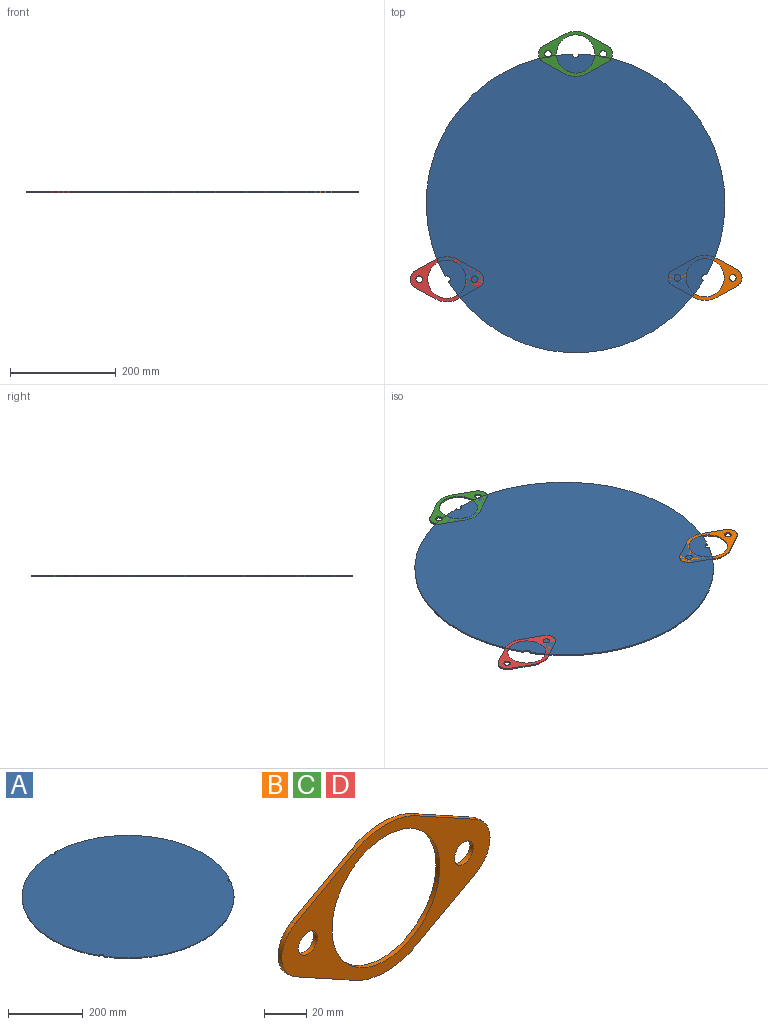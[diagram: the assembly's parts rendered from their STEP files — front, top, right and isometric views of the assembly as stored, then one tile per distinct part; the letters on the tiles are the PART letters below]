
ASSEMBLY  parts=4 mates=5
PART A: 8 faces, bbox 565.8x565.7x2.5 mm
  f0: cylinder r=6.35mm len=11.82mm, axis (0,0,-1), area 50.3mm2, adj f1,f5,f6,f7
  f1: cylinder r=282.91mm len=418.29mm, axis (0,0,-1), area 1471.4mm2, adj f0,f2,f6,f7
  f2: cylinder r=6.35mm len=12.7mm, axis (0,0,-1), area 50.3mm2, adj f1,f3,f6,f7
  f3: cylinder r=282.91mm len=421.07mm, axis (0,0,-1), area 1479.5mm2, adj f2,f4,f6,f7
  f4: cylinder r=6.35mm len=11.78mm, axis (0,0,-1), area 50.3mm2, adj f3,f5,f6,f7
  f5: cylinder r=282.91mm len=482.44mm, axis (0,0,-1), area 1467.4mm2, adj f0,f4,f6,f7
  f6: plane 565.82x565.75mm, normal (0,0,1), area 251257.3mm2, adj f0,f1,f2,f3,f4,f5
  f7: plane 565.82x565.75mm, normal (0,0,-1), area 251257.3mm2, adj f0,f1,f2,f3,f4,f5
PART B: 13 faces, bbox 139.7x2.5x85.6 mm
  f0: cylinder r=17.53mm len=30.69mm, axis (0,1,0), area 95mm2, adj f1,f9,f11,f12
  f1: plane 40.12x22.13mm, normal (0.48,0,0.88), area 116.4mm2, adj f0,f2,f11,f12
  f2: cylinder r=42.8mm len=41.34mm, axis (0,1,0), area 109.6mm2, adj f1,f3,f11,f12
  f3: plane 40.12x22.13mm, normal (-0.48,0,0.88), area 116.4mm2, adj f2,f4,f11,f12
  f4: cylinder r=17.53mm len=30.69mm, axis (0,1,0), area 95mm2, adj f3,f5,f11,f12
  f5: plane 40.12x22.13mm, normal (-0.48,0,-0.88), area 116.4mm2, adj f4,f6,f11,f12
  f6: cylinder r=42.8mm len=41.34mm, axis (0,1,0), area 109.6mm2, adj f5,f9,f11,f12
  f7: cylinder r=6.35mm len=12.7mm, axis (0,1,0), area 101.3mm2, adj f11,f12
  f8: cylinder r=6.35mm len=12.7mm, axis (0,1,0), area 101.3mm2, adj f11,f12
  f9: plane 40.12x22.13mm, normal (0.48,0,-0.88), area 116.4mm2, adj f0,f6,f11,f12
  f10: cylinder r=36.2mm len=72.39mm, axis (0,1,0), area 577.6mm2, adj f11,f12
  f11: plane 139.7x85.6mm, normal (0,-1,0), area 3660.6mm2, adj f0,f1,f2,f3,f4,f5,f6,f7
  f12: plane 139.7x85.6mm, normal (0,1,0), area 3660.6mm2, adj f0,f1,f2,f3,f4,f5,f6,f7
PART C: same geometry as B
PART D: same geometry as B
PLACE A t=(0,0,-2.54)mm fixed
PLACE B rot(axis=(-1,0,0),90deg) t=(245.28,-140.99,-2.54)mm
PLACE C rot(axis=(-1,0,0),90deg) t=(0,282.91,-2.54)mm
PLACE D rot(axis=(-1,0,0),90deg) t=(-243.67,-143.74,-2.54)mm
MATE planar B.f2 <-> C.f2  axis (0,0,1) through (245.28,-140.99,0)mm
MATE revolute A.f2 <-> C.f2  axis (0,0,1) through (0,282.91,0)mm
MATE revolute B.f2 <-> A.f0  axis (0,0,1) through (245.28,-140.99,0)mm
MATE revolute D.f2 <-> A.f4  axis (0,0,1) through (-243.67,-143.74,0)mm
MATE planar C.f2 <-> D.f2  axis (0,0,1) through (0,282.91,0)mm
